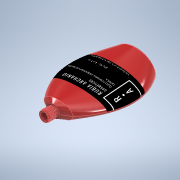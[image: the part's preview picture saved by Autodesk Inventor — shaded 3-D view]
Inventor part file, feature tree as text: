
AUTODESK INVENTOR PART (.ipt)
format: ipt  version: 2021 (Build 250183000, 183)  size: 1,670,656 bytes
history: native  units: mm
features: other x11, sketch x10, loft x2, extrude x2, fillet x1, shell x1
ambient origin geometry x8: Origin, YZ Plane, XZ Plane, XY Plane, X Axis, Y Axis, Z Axis, Center Point
bodies: Body1 (feature_tree)
feature tree (27):
  other  "Sólido1"
  sketch  "Esboço1"  dims[d0=60.0mm d2=80.0mm]
  other  "Plano de trabalho1"
  sketch  "Esboço2"  dims[d3=120.0mm d4=40.0mm]
  other  "Plano de trabalho2"
  sketch  "Esboço3"  dims[d5=130.0mm d6=200.0mm d7=30.0mm d8=60.0mm]
  other  "Plano de trabalho3"
  sketch  "Esboço4"  dims[d9=20.0mm d10=50.0mm]
  loft  "Transição1"
  loft  "Transição2"
  extrude  "Extrusão1"  Depth=200.0mm
  fillet  "Arredondamento1"  Radius=30.0mm
  shell  "Casca1"  Thickness=60.0mm
  extrude  "Extrusão2"  Depth=50.0mm
  other  "Espiral1"
  other  "Decalque1"
  other  "Plano de trabalho4"
  other  "Relevo1"
  other  "Relevo2"
  other  "Arestas1"
  sketch  "Esboço5"  dims[d11=0.0mm d12=90.0deg]
  sketch  "Esboço6"  dims[d13=0.0mm d14=90.0deg]
  sketch  "Esboço7"  dims[d15=0.0mm d16=90.0deg]
  sketch  "Esboço8"  dims[d17=0.0mm d18=90.0deg]
  other  "Imagem1"
  sketch  "Esboço9"  dims[d19=0.0mm d20=90.0deg]
  sketch  "Esboço10"  dims[d21=40.0mm d22=60.0mm d23=10.0mm d24=0.0mm d25=4.0mm d26=5.0mm d27=30.0mm d28=40.0mm d29=40.0mm d30=0.0mm d31=3.0mm d32=3.0mm d33=6.0mm d34=10.0mm d35=55.0mm d36=0.0mm d37=90.0deg d38=90.0deg d39=0.0mm d40=0.0mm d50=-60.0mm d51=1.0mm d52=0.0mm d53=1.0mm d54=0.0mm]
